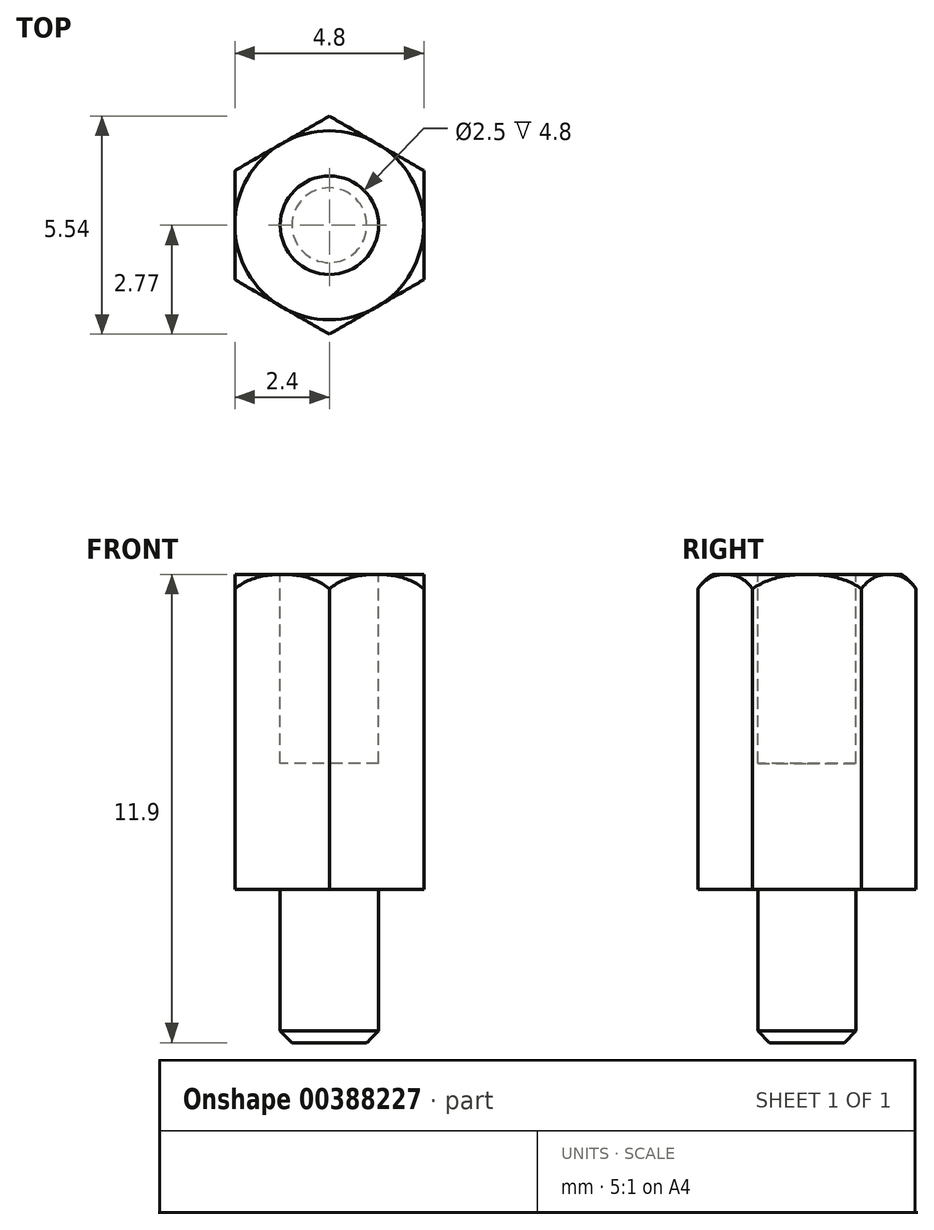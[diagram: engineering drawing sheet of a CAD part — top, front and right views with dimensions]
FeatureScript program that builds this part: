
annotation { "Feature Type Name" : "Feature", "Feature Type Description" : "" }
export const myFeature = defineFeature(function(context is Context, id is Id, definition is map)
    precondition{}
    {
        {
            var Q0;
            Q0=qCreatedBy(makeId("Top.planeOp"),FACE);
            var sketch = newSketch(context, id + "F0", { "sketchPlane" : qUnion([Q0])});
            skCircle(sketch, "E0", {"center": v(0, 0) * mm, "radius": 1.25 * mm});
            skSolve(sketch);
        }
        {
            var Q0;
            Q0=makeQuery(id+"F0.imprint","IMPRINT",FACE,{"disambiguationData":[TD([[makeQuery(id+"F0.imprint","IMPRINT",EDGE,{"derivedFrom":sQuery(id+"F0.wireOp",EDGE,"E0")}),1.0]])]});
            extrude(context, id + "F1", {"entities" : qUnion([Q0]), "depth" : 3.9 * mm});
        }
        {
            var Q0;
            Q0=makeQuery(id+"F1.opExtrude","CAP_FACE",FACE,{"disambiguationData":[OSD([sQuery(id+"F0.wireOp",EDGE,"E0")])],"isStart":false});
            var sketch = newSketch(context, id + "F2", { "sketchPlane" : qUnion([Q0])});
            skCircle(sketch, "E1.cCircle", {"center": v(0, 0) * mm, "radius": 2.4 * mm, "construction": true});
            skLineSegment(sketch, "E1.0", {"start": v(0, 2.77) * mm, "end": v(2.4, 1.39) * mm});
            skLineSegment(sketch, "E1.1", {"start": v(2.4, 1.39) * mm, "end": v(2.4, -1.39) * mm});
            skLineSegment(sketch, "E1.2", {"start": v(2.4, -1.39) * mm, "end": v(0, -2.77) * mm});
            skLineSegment(sketch, "E1.3", {"start": v(0, -2.77) * mm, "end": v(-2.4, -1.39) * mm});
            skLineSegment(sketch, "E1.4", {"start": v(-2.4, -1.39) * mm, "end": v(-2.4, 1.39) * mm});
            skLineSegment(sketch, "E1.5", {"start": v(-2.4, 1.39) * mm, "end": v(0, 2.77) * mm});
            skPoint(sketch, "E1.0.midPoint", {"position": v(1.2, 2.08) * mm});
            skSolve(sketch);
        }
        {
            var Q0;
            Q0 = qSketchRegion(id + "F2", true);
            extrude(context, id + "F3", {"entities" : qUnion([Q0]), "operationType" : NewBodyOperationType.ADD, "depth" : 8 * mm});
        }
        {
            var Q0;
            Q0=makeQuery(id+"F3.opExtrude","CAP_FACE",FACE,{"disambiguationData":[OSD([sQuery(id+"F2.wireOp",EDGE,"E1.0"),sQuery(id+"F2.wireOp",EDGE,"E1.1"),sQuery(id+"F2.wireOp",EDGE,"E1.2"),sQuery(id+"F2.wireOp",EDGE,"E1.3"),sQuery(id+"F2.wireOp",EDGE,"E1.4"),sQuery(id+"F2.wireOp",EDGE,"E1.5")])],"isStart":false});
            var sketch = newSketch(context, id + "F4", { "sketchPlane" : qUnion([Q0])});
            skCircle(sketch, "E2", {"center": v(0, 0) * mm, "radius": 1.25 * mm});
            skSolve(sketch);
        }
        {
            var Q0;
            Q0=makeQuery(id+"F4.imprint","IMPRINT",FACE,{"disambiguationData":[TD([[makeQuery(id+"F4.imprint","IMPRINT",EDGE,{"derivedFrom":sQuery(id+"F4.wireOp",EDGE,"E2")}),1.0]])]});
            extrude(context, id + "F5", {"entities" : qUnion([Q0]), "operationType" : NewBodyOperationType.REMOVE, "oppositeDirection" : true, "depth" : 4.8 * mm});
        }
        {
            var Q0;
            Q0=makeQuery(id+"F3.opExtrude","CAP_FACE",FACE,{"disambiguationData":[OSD([sQuery(id+"F2.wireOp",EDGE,"E1.0"),sQuery(id+"F2.wireOp",EDGE,"E1.1"),sQuery(id+"F2.wireOp",EDGE,"E1.2"),sQuery(id+"F2.wireOp",EDGE,"E1.3"),sQuery(id+"F2.wireOp",EDGE,"E1.4"),sQuery(id+"F2.wireOp",EDGE,"E1.5")])],"isStart":false});
            var sketch = newSketch(context, id + "F6", { "sketchPlane" : qUnion([Q0])});
            skCircle(sketch, "E3", {"center": v(0, 0) * mm, "radius": 2.4 * mm});
            skSolve(sketch);
        }
        {
            var Q0;
            Q0=qCreatedBy(makeId("Right.planeOp"),FACE);
            var sketch = newSketch(context, id + "F7", { "sketchPlane" : qUnion([Q0])});
            skLineSegment(sketch, "E4.0", {"start": v(-2.4, 11.9) * mm, "end": v(2.4, 11.9) * mm, "construction": true});
            skLineSegment(sketch, "E5", {"start": v(2.4, 11.9) * mm, "end": v(2.77, 11.53) * mm, "construction": true});
            skPoint(sketch, "E6.0", {"position": v(2.77, 11.9) * mm});
            skArc(sketch, "E7", {"start": v(2.77, 11.53) * mm, "mid": v(2.6, 11.73) * mm, "end": v(2.4, 11.9) * mm});
            skLineSegment(sketch, "E8", {"start": v(2.4, 11.9) * mm, "end": v(2.77, 11.9) * mm});
            skLineSegment(sketch, "E9", {"start": v(2.77, 11.9) * mm, "end": v(2.77, 11.53) * mm});
            skSolve(sketch);
        }
        {
            var Q0;
            Q0 = qSketchRegion(id + "F7", true);
            var Q1;
            Q1=sQuery(id+"F6.wireOp",EDGE,"E3");
            revolve(context, id + "F8", {"operationType" : NewBodyOperationType.REMOVE, "entities" : qUnion([Q0]), "axis" : qUnion([Q1]), "revolveType" : RevolveType.FULL, "oppositeDirection" : true});
        }
        {
            var Q0;
            Q0=makeQuery(id+"F3.opExtrude","CAP_FACE",FACE,{"disambiguationData":[OSD([sQuery(id+"F2.wireOp",EDGE,"E1.0"),sQuery(id+"F2.wireOp",EDGE,"E1.1"),sQuery(id+"F2.wireOp",EDGE,"E1.2"),sQuery(id+"F2.wireOp",EDGE,"E1.3"),sQuery(id+"F2.wireOp",EDGE,"E1.4"),sQuery(id+"F2.wireOp",EDGE,"E1.5")])],"isStart":true});
            cPlane(context, id + "F9", {"entities" : qUnion([Q0]), "cplaneType" : CPlaneType.OFFSET, "offset" : 4 * mm, "oppositeDirection" : true, "width" : 150 * mm, "height" : 150 * mm});
        }
        {
            var Q0;
            Q0=makeQuery(id+"F1.opExtrude","CAP_EDGE",EDGE,{"disambiguationData":[OSD([sQuery(id+"F0.wireOp",EDGE,"E0")])],"isStart":true});
            chamfer(context, id + "F10", {"entities" : qUnion([Q0]), "width" : .3 * mm, "tangentPropagation" : true});
        }
    });
